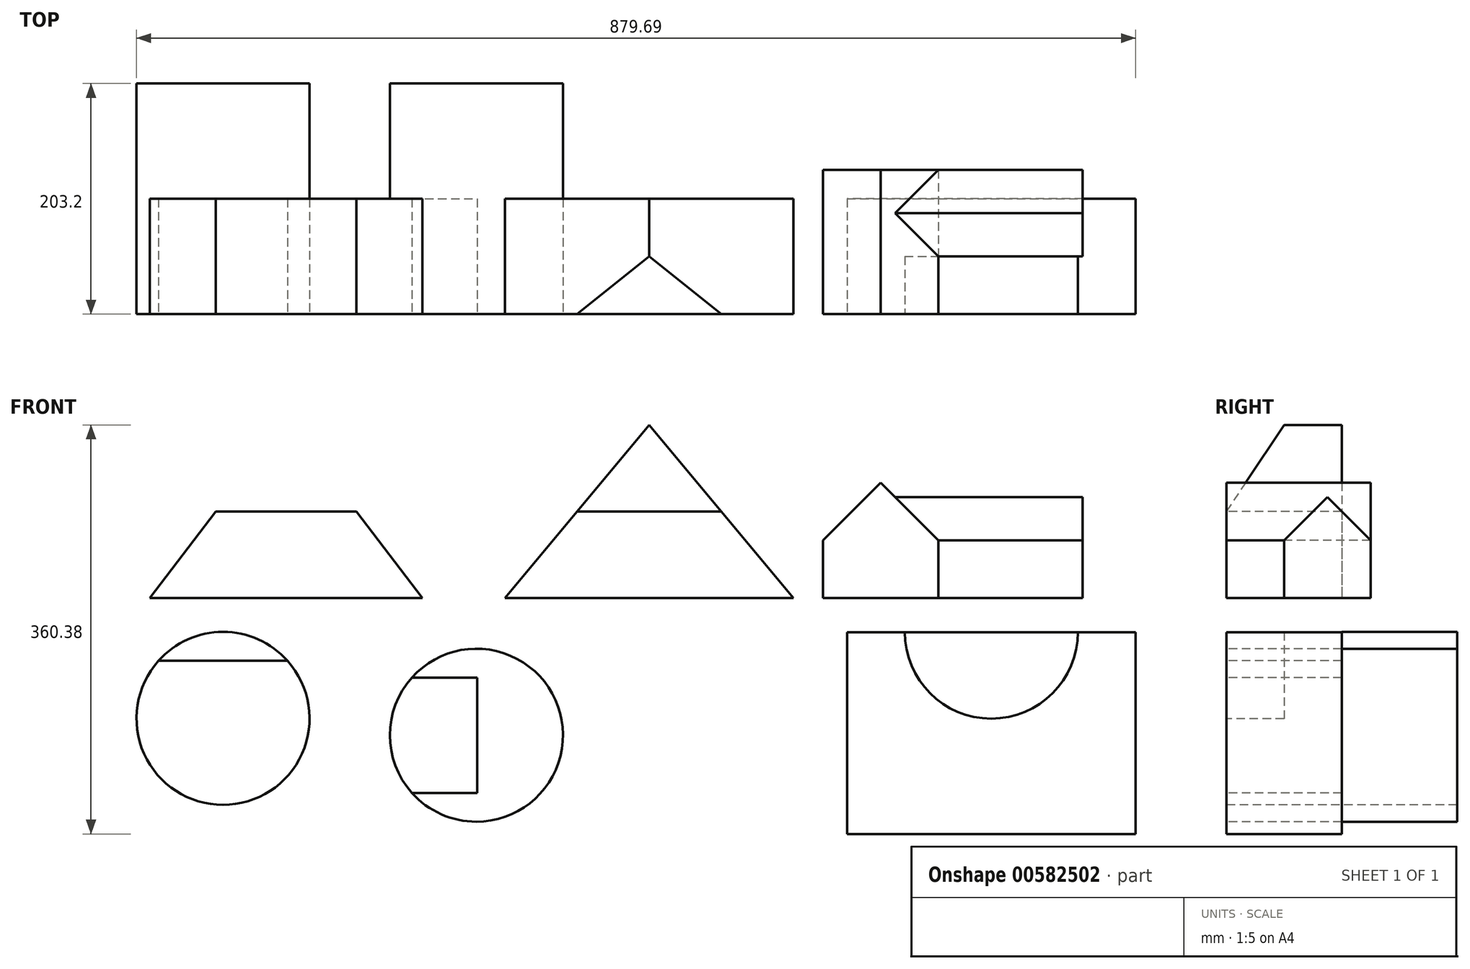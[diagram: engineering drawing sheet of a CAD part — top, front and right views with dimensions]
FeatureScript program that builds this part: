
annotation { "Feature Type Name" : "Feature", "Feature Type Description" : "" }
export const myFeature = defineFeature(function(context is Context, id is Id, definition is map)
    precondition{}
    {
        {
            var Q0;
            Q0=qCreatedBy(makeId("Front.planeOp"),FACE);
            var sketch = newSketch(context, id + "F0", { "sketchPlane" : qUnion([Q0])});
            skLineSegment(sketch, "E0", {"start": v(-64.46, 0) * mm, "end": v(175.6, 0) * mm});
            skLineSegment(sketch, "E1", {"start": v(55.57, 157.4) * mm, "end": v(-64.46, 0) * mm});
            skLineSegment(sketch, "E2", {"start": v(55.57, 157.4) * mm, "end": v(175.6, 0) * mm});
            skLineSegment(sketch, "E3", {"start": v(117.5, 76.2) * mm, "end": v(-6.35, 76.2) * mm});
            skLineSegment(sketch, "E4", {"start": v(-6.35, 76.2) * mm, "end": v(55.57, 157.4) * mm});
            skSolve(sketch);
        }
        {
            var Q0;
            {var subQ0=sQuery(id+"F0.wireOp",EDGE,"E0");Q0=makeQuery(id+"F0.imprint","IMPRINT",FACE,{"disambiguationData":[TD([[makeQuery(id+"F0.imprint","IMPRINT",EDGE,{"derivedFrom":subQ0}),1.0]])]});}
            var Q1;
            {var subQ0=sQuery(id+"F0.wireOp",EDGE,"E4");Q1=makeQuery(id+"F0.imprint","IMPRINT",FACE,{"disambiguationData":[TD([[makeQuery(id+"F0.imprint","IMPRINT",EDGE,{"derivedFrom":subQ0}),-1.0]])]});}
            extrude(context, id + "F1", {"entities" : qUnion([Q0, Q1]), "oppositeDirection" : true, "depth" : 101.6 * mm, "offsetDistance" : 25.4 * mm});
        }
        {
            var Q0;
            Q0=makeQuery(id+"F1.opExtrude","CAP_FACE",FACE,{"disambiguationData":[OSD([sQuery(id+"F0.wireOp",EDGE,"E0"),sQuery(id+"F0.wireOp",EDGE,"E1"),sQuery(id+"F0.wireOp",EDGE,"E2"),sQuery(id+"F0.wireOp",EDGE,"E4")])],"isStart":true});
            var sketch = newSketch(context, id + "F2", { "sketchPlane" : qUnion([Q0])});
            skLineSegment(sketch, "E5", {"start": v(115.59, 78.7) * mm, "end": v(-4.44, 78.7) * mm});
            skLineSegment(sketch, "E6", {"start": v(-4.44, 78.7) * mm, "end": v(55.57, 157.4) * mm});
            skLineSegment(sketch, "E7", {"start": v(55.57, 157.4) * mm, "end": v(115.59, 78.7) * mm});
            skSolve(sketch);
        }
        {
            var Q0;
            Q0=makeQuery(id+"F2.imprint","IMPRINT",FACE,{"disambiguationData":[TD([[makeQuery(id+"F2.imprint","IMPRINT",EDGE,{"derivedFrom":sQuery(id+"F2.wireOp",EDGE,"E5")}),-1.0]])]});
            extrude(context, id + "F3", {"entities" : qUnion([Q0]), "operationType" : NewBodyOperationType.REMOVE, "oppositeDirection" : true, "depth" : 50.8 * mm, "offsetDistance" : 25.4 * mm});
        }
        {
            var Q0;
            Q0=qCreatedBy(makeId("Front.planeOp"),FACE);
            var sketch = newSketch(context, id + "F4", { "sketchPlane" : qUnion([Q0])});
            skLineSegment(sketch, "E8", {"start": v(502.37, 0) * mm, "end": v(248.37, 0) * mm});
            skLineSegment(sketch, "E9", {"start": v(248.37, 0) * mm, "end": v(375.37, 152.4) * mm});
            skLineSegment(sketch, "E10", {"start": v(375.37, 152.4) * mm, "end": v(502.37, 0) * mm});
            skSolve(sketch);
        }
        {
            var Q0;
            Q0=makeQuery(id+"F4.imprint","IMPRINT",FACE,{"disambiguationData":[TD([[makeQuery(id+"F4.imprint","IMPRINT",EDGE,{"derivedFrom":sQuery(id+"F4.wireOp",EDGE,"E8")}),-1.0]])]});
            extrude(context, id + "F5", {"entities" : qUnion([Q0]), "oppositeDirection" : true, "depth" : 101.6 * mm, "offsetDistance" : 25.4 * mm});
        }
        {
            var Q0;
            Q0=makeQuery(id+"F5.opExtrude","CAP_FACE",FACE,{"disambiguationData":[OSD([sQuery(id+"F4.wireOp",EDGE,"E8"),sQuery(id+"F4.wireOp",EDGE,"E9"),sQuery(id+"F4.wireOp",EDGE,"E10")])],"isStart":true});
            var sketch = newSketch(context, id + "F6", { "sketchPlane" : qUnion([Q0])});
            skLineSegment(sketch, "E11", {"start": v(311.87, 76.2) * mm, "end": v(438.87, 76.2) * mm});
            skLineSegment(sketch, "E12", {"start": v(438.87, 76.2) * mm, "end": v(375.37, 152.4) * mm});
            skLineSegment(sketch, "E13", {"start": v(375.37, 152.4) * mm, "end": v(311.87, 76.2) * mm});
            skSolve(sketch);
        }
        {
            var Q0;
            Q0=makeQuery(id+"F5.opExtrude","CAP_EDGE",EDGE,{"disambiguationData":[OSD([sQuery(id+"F4.wireOp",EDGE,"E8")])],"isStart":true});
            cPoint(context, id + "F7", {"entities" : qUnion([Q0]), "parameter" : 0.5});
        }
        {
            var Q0;
            Q0=sQuery(id+"F6.wireOp",VERTEX,"E13.start");
            var Q1;
            Q1=makeQuery(id+"F5.opExtrude","CAP_VERTEX",VERTEX,{"disambiguationData":[OSD([sQuery(id+"F4.wireOp",EDGE,"E9"),sQuery(id+"F4.wireOp",EDGE,"E10")])],"isStart":false});
            var Q2;
            Q2 = qCreatedBy(id + "F7" ,VERTEX);
            cPlane(context, id + "F8", {"entities" : qUnion([Q0, Q1, Q2]), "cplaneType" : CPlaneType.THREE_POINT, "offset" : 25.4 * mm, "width" : 152.4 * mm, "height" : 152.4 * mm});
        }
        {
            var Q0;
            Q0=qCreatedBy(id+"F8.planeOp",FACE);
            var sketch = newSketch(context, id + "F9", { "sketchPlane" : qUnion([Q0])});
            skLineSegment(sketch, "E14", {"start": v(0, 152.4) * mm, "end": v(0, 76.2) * mm});
            skLineSegment(sketch, "E15", {"start": v(0, 76.2) * mm, "end": v(50.8, 152.4) * mm});
            skLineSegment(sketch, "E16", {"start": v(50.8, 152.4) * mm, "end": v(0, 152.4) * mm});
            skSolve(sketch);
        }
        {
            var Q0;
            Q0 = qSketchRegion(id + "F9", true);
            extrude(context, id + "F10", {"entities" : qUnion([Q0]), "operationType" : NewBodyOperationType.REMOVE, "endBound" : BoundingType.SYMMETRIC, "oppositeDirection" : true, "depth" : 152.4 * mm, "offsetDistance" : 25.4 * mm});
        }
        {
            var Q0;
            Q0=qCreatedBy(makeId("Front.planeOp"),FACE);
            var sketch = newSketch(context, id + "F11", { "sketchPlane" : qUnion([Q0])});
            skLineSegment(sketch, "E17", {"start": v(528.12, 50.8) * mm, "end": v(528.12, 0) * mm});
            skLineSegment(sketch, "E18", {"start": v(528.12, 0) * mm, "end": v(629.72, 0) * mm});
            skLineSegment(sketch, "E19", {"start": v(629.72, 0) * mm, "end": v(629.72, 50.8) * mm});
            skLineSegment(sketch, "E20", {"start": v(629.72, 50.8) * mm, "end": v(578.92, 101.6) * mm});
            skLineSegment(sketch, "E21", {"start": v(578.92, 101.6) * mm, "end": v(528.12, 50.8) * mm});
            skSolve(sketch);
        }
        {
            var Q0;
            Q0=makeQuery(id+"F11.imprint","IMPRINT",FACE,{"disambiguationData":[TD([[makeQuery(id+"F11.imprint","IMPRINT",EDGE,{"derivedFrom":sQuery(id+"F11.wireOp",EDGE,"E17")}),1.0]])]});
            extrude(context, id + "F12", {"entities" : qUnion([Q0]), "oppositeDirection" : true, "depth" : 127 * mm, "offsetDistance" : 25.4 * mm});
        }
        {
            var Q0;
            Q0=makeQuery(id+"F12.opExtrude","SWEPT_FACE",FACE,{"disambiguationData":[OSD([sQuery(id+"F11.wireOp",EDGE,"E19")])]});
            cPlane(context, id + "F13", {"entities" : qUnion([Q0]), "cplaneType" : CPlaneType.OFFSET, "offset" : 127 * mm, "width" : 152.4 * mm, "height" : 152.4 * mm});
        }
        {
            var Q0;
            Q0=qCreatedBy(id+"F13.planeOp",FACE);
            var sketch = newSketch(context, id + "F14", { "sketchPlane" : qUnion([Q0])});
            skLineSegment(sketch, "E22", {"start": v(127, 0) * mm, "end": v(50.8, 0) * mm});
            skLineSegment(sketch, "E23", {"start": v(50.8, 0) * mm, "end": v(50.8, 50.8) * mm});
            skLineSegment(sketch, "E24", {"start": v(50.8, 50.8) * mm, "end": v(88.9, 88.9) * mm});
            skLineSegment(sketch, "E25", {"start": v(88.9, 88.9) * mm, "end": v(127, 50.8) * mm});
            skLineSegment(sketch, "E26", {"start": v(127, 50.8) * mm, "end": v(127, 0) * mm});
            skSolve(sketch);
        }
        {
            var Q0;
            Q0=makeQuery(id+"F14.imprint","IMPRINT",FACE,{"disambiguationData":[TD([[makeQuery(id+"F14.imprint","IMPRINT",EDGE,{"derivedFrom":sQuery(id+"F14.wireOp",EDGE,"E22")}),-1.0]])]});
            extrude(context, id + "F15", {"entities" : qUnion([Q0]), "endBound" : BoundingType.UP_TO_NEXT, "oppositeDirection" : true, "depth" : 25.4 * mm, "offsetDistance" : 25.4 * mm});
        }
        {
            var Q0;
            Q0=qCreatedBy(makeId("Front.planeOp"),FACE);
            var sketch = newSketch(context, id + "F16", { "sketchPlane" : qUnion([Q0])});
            skCircle(sketch, "E27", {"center": v(0, -106.17) * mm, "radius": 76.2 * mm});
            skSolve(sketch);
        }
        {
            var Q0;
            Q0=makeQuery(id+"F16.imprint","IMPRINT",FACE,{"disambiguationData":[TD([[makeQuery(id+"F16.imprint","IMPRINT",EDGE,{"derivedFrom":sQuery(id+"F16.wireOp",EDGE,"E27")}),1.0]])]});
            extrude(context, id + "F17", {"entities" : qUnion([Q0]), "oppositeDirection" : true, "depth" : 203.2 * mm, "offsetDistance" : 25.4 * mm});
        }
        {
            var Q0;
            Q0=makeQuery(id+"F17.opExtrude","CAP_FACE",FACE,{"disambiguationData":[OSD([sQuery(id+"F16.wireOp",EDGE,"E27")])],"isStart":true});
            var sketch = newSketch(context, id + "F18", { "sketchPlane" : qUnion([Q0])});
            skLineSegment(sketch, "E28", {"start": v(-56.8, -55.37) * mm, "end": v(56.8, -55.37) * mm});
            skSolve(sketch);
        }
        {
            var Q0;
            {var subQ0=sQuery(id+"F18.wireOp",EDGE,"E28");Q0=makeQuery(id+"F18.imprint","IMPRINT",FACE,{"disambiguationData":[TD([[makeQuery(id+"F18.imprint","IMPRINT",EDGE,{"derivedFrom":subQ0}),1.0]])]});}
            extrude(context, id + "F19", {"entities" : qUnion([Q0]), "operationType" : NewBodyOperationType.REMOVE, "oppositeDirection" : true, "depth" : 101.6 * mm, "offsetDistance" : 25.4 * mm});
        }
        {
            var Q0;
            Q0=qCreatedBy(makeId("Front.planeOp"),FACE);
            var sketch = newSketch(context, id + "F20", { "sketchPlane" : qUnion([Q0])});
            skCircle(sketch, "E29", {"center": v(223.1, -121.02) * mm, "radius": 76.2 * mm});
            skSolve(sketch);
        }
        {
            var Q0;
            Q0=makeQuery(id+"F20.imprint","IMPRINT",FACE,{"disambiguationData":[TD([[makeQuery(id+"F20.imprint","IMPRINT",EDGE,{"derivedFrom":sQuery(id+"F20.wireOp",EDGE,"E29")}),1.0]])]});
            extrude(context, id + "F21", {"entities" : qUnion([Q0]), "oppositeDirection" : true, "depth" : 203.2 * mm, "offsetDistance" : 25.4 * mm});
        }
        {
            var Q0;
            Q0=makeQuery(id+"F21.opExtrude","CAP_FACE",FACE,{"disambiguationData":[OSD([sQuery(id+"F20.wireOp",EDGE,"E29")])],"isStart":true});
            var sketch = newSketch(context, id + "F22", { "sketchPlane" : qUnion([Q0])});
            skLineSegment(sketch, "E30", {"start": v(166.3, -70.22) * mm, "end": v(223.89, -70.22) * mm});
            skLineSegment(sketch, "E31", {"start": v(223.89, -70.22) * mm, "end": v(223.89, -171.82) * mm});
            skLineSegment(sketch, "E32", {"start": v(223.89, -171.82) * mm, "end": v(166.3, -171.82) * mm});
            skSolve(sketch);
        }
        {
            var Q0;
            {var subQ0=sQuery(id+"F22.wireOp",EDGE,"E30");Q0=makeQuery(id+"F22.imprint","IMPRINT",FACE,{"disambiguationData":[TD([[makeQuery(id+"F22.imprint","IMPRINT",EDGE,{"derivedFrom":subQ0}),-1.0]])]});}
            extrude(context, id + "F23", {"entities" : qUnion([Q0]), "operationType" : NewBodyOperationType.REMOVE, "oppositeDirection" : true, "depth" : 101.6 * mm, "offsetDistance" : 25.4 * mm});
        }
        {
            var Q0;
            Q0=qCreatedBy(makeId("Front.planeOp"),FACE);
            var sketch = newSketch(context, id + "F24", { "sketchPlane" : qUnion([Q0])});
            skLineSegment(sketch, "E33", {"start": v(549.5, -207.98) * mm, "end": v(549.5, -30.18) * mm});
            skLineSegment(sketch, "E34", {"start": v(549.5, -30.18) * mm, "end": v(803.5, -30.18) * mm});
            skLineSegment(sketch, "E35", {"start": v(803.5, -30.18) * mm, "end": v(803.5, -207.98) * mm});
            skLineSegment(sketch, "E36", {"start": v(803.5, -207.98) * mm, "end": v(549.5, -207.98) * mm});
            skSolve(sketch);
        }
        {
            var Q0;
            Q0=makeQuery(id+"F24.imprint","IMPRINT",FACE,{"disambiguationData":[TD([[makeQuery(id+"F24.imprint","IMPRINT",EDGE,{"derivedFrom":sQuery(id+"F24.wireOp",EDGE,"E33")}),-1.0]])]});
            extrude(context, id + "F25", {"entities" : qUnion([Q0]), "oppositeDirection" : true, "depth" : 101.6 * mm, "offsetDistance" : 25.4 * mm});
        }
        {
            var Q0;
            Q0=makeQuery(id+"F25.opExtrude","CAP_FACE",FACE,{"disambiguationData":[OSD([sQuery(id+"F24.wireOp",EDGE,"E33"),sQuery(id+"F24.wireOp",EDGE,"E34"),sQuery(id+"F24.wireOp",EDGE,"E35"),sQuery(id+"F24.wireOp",EDGE,"E36")])],"isStart":true});
            var sketch = newSketch(context, id + "F26", { "sketchPlane" : qUnion([Q0])});
            skCircle(sketch, "E37", {"center": v(676.5, -30.18) * mm, "radius": 76.2 * mm});
            skSolve(sketch);
        }
        {
            var Q0;
            {var subQ0=sQuery(id+"F26.wireOp",EDGE,"E37");var subQ1=makeQuery(id+"F25.opExtrude","CAP_EDGE",EDGE,{"disambiguationData":[OSD([sQuery(id+"F24.wireOp",EDGE,"E34")])],"isStart":true});var subQ2=makeQuery(id+"F26.imprint","INTERSECT",VERTEX,{"disambiguationData":[OD(0.0)],"derivedFrom":[subQ1,subQ0]});Q0=makeQuery(id+"F26.imprint","IMPRINT",FACE,{"disambiguationData":[TD([[makeQuery(id+"F26.imprint","IMPRINT",EDGE,{"disambiguationData":[TD([[subQ2,-1.0]])],"derivedFrom":subQ0}),1.0]])]});}
            extrude(context, id + "F27", {"entities" : qUnion([Q0]), "operationType" : NewBodyOperationType.REMOVE, "oppositeDirection" : true, "depth" : 50.8 * mm, "offsetDistance" : 25.4 * mm});
        }
    });
